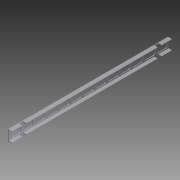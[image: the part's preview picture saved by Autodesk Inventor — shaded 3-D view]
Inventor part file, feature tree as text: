
AUTODESK INVENTOR PART (.ipt)
format: ipt  version: 2012 (Build 160160000, 160)  size: 261,632 bytes
history: native  units: in
note: dims shown in document units (in); Inventor stores cm internally (conversion verified against a paired STEP export)
features: extrude x3, sketch x3
ambient origin geometry x8: Origin, YZ Plane, XZ Plane, XY Plane, X Axis, Y Axis, Z Axis, Center Point
bodies: Solid1 (feature_tree)
feature tree (6):
  extrude  "Extrusion1"  Depth=35.0in TaperAngle=0.0deg
  extrude  "Extrusion4"  Depth=0.875in
  extrude  "Extrusion5"  Depth=35.0in
  sketch  "Sketch1"  dims[d0=0.125in d1=0.125in d2=0.125in d3=2.25in d4=0.875in d5=35.0in d6=0.0in]
  sketch  "Sketch4"  dims[d33=0.75in d34=0.875in]
  sketch  "Sketch5"  dims[d35=3.125in d36=35.0in d37=17.5in d38=1.0in d39=0.0in d40=0.375in d41=0.375in d42=0.375in d43=0.375in d44=3.0in d45=0.1875in d46=0.375in d47=0.1875in d48=2.6635in d49=0.25in d50=5.1181in d52=2.6635in d53=0.3937in d55=1.0in d57=1.0in d58=0.0in]
